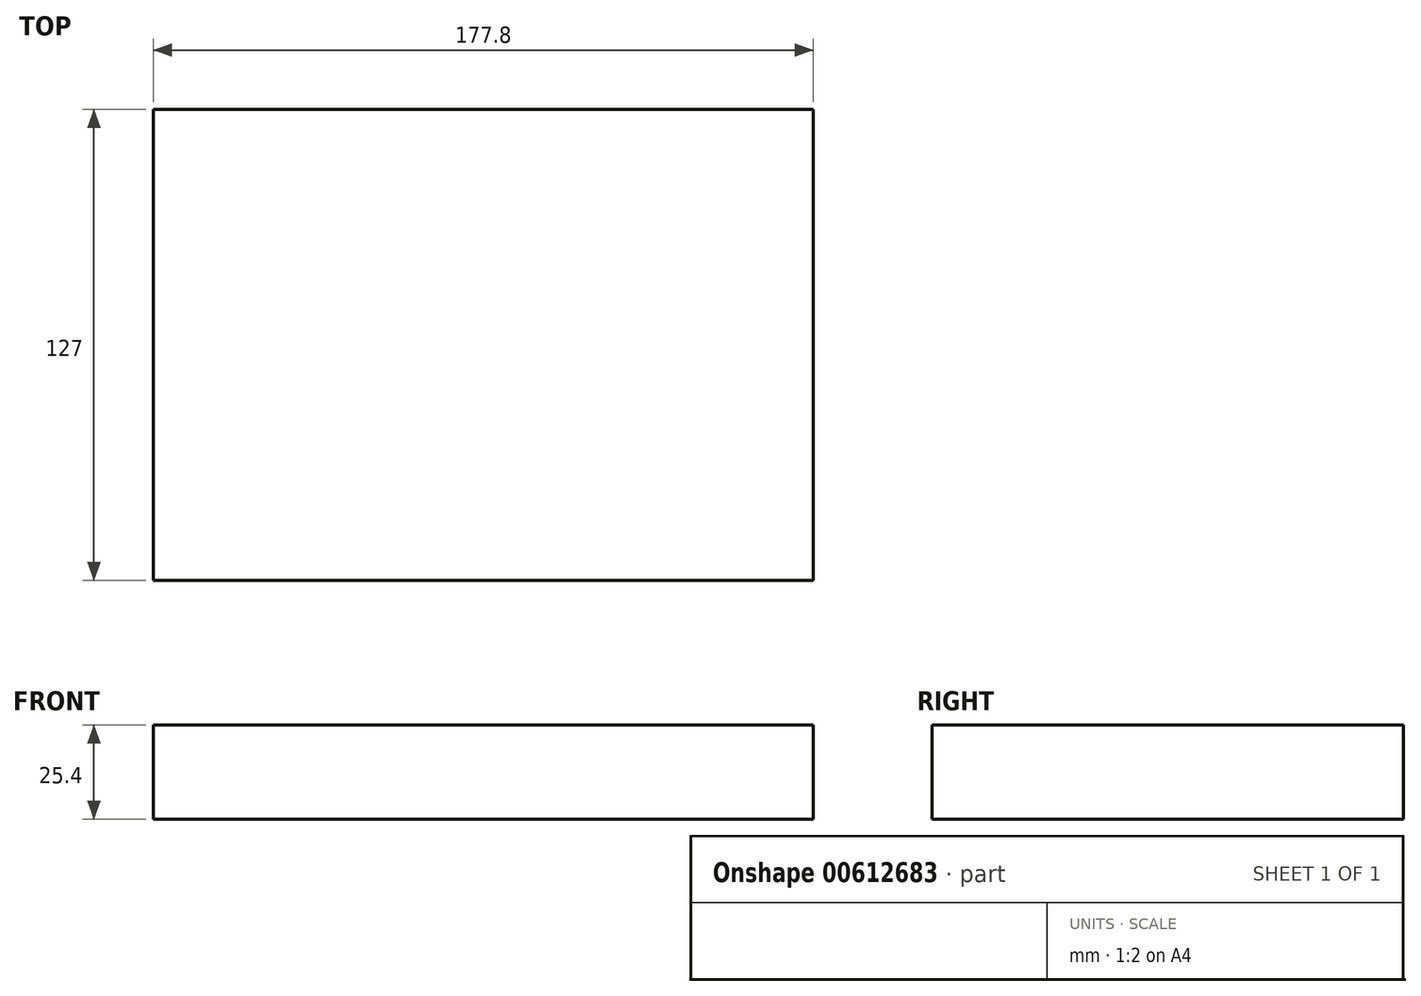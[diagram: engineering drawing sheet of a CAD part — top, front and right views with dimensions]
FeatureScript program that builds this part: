
annotation { "Feature Type Name" : "Feature", "Feature Type Description" : "" }
export const myFeature = defineFeature(function(context is Context, id is Id, definition is map)
    precondition{}
    {
        {
            var Q0;
            Q0=qCreatedBy(makeId("Top.planeOp"),FACE);
            var sketch = newSketch(context, id + "F0", { "sketchPlane" : qUnion([Q0])});
            skLineSegment(sketch, "E0.bottom", {"start": v(88.9, 63.5) * mm, "end": v(-88.9, 63.5) * mm});
            skLineSegment(sketch, "E0.top", {"start": v(88.9, -63.5) * mm, "end": v(-88.9, -63.5) * mm});
            skLineSegment(sketch, "E0.left", {"start": v(88.9, 63.5) * mm, "end": v(88.9, -63.5) * mm});
            skLineSegment(sketch, "E0.right", {"start": v(-88.9, 63.5) * mm, "end": v(-88.9, -63.5) * mm});
            skPoint(sketch, "E0.middle", {"position": v(0, 0) * mm});
            skSolve(sketch);
        }
        {
            var Q0;
            Q0=makeQuery(id+"F0.imprint","IMPRINT",FACE,{"disambiguationData":[TD([[makeQuery(id+"F0.imprint","IMPRINT",EDGE,{"derivedFrom":sQuery(id+"F0.wireOp",EDGE,"E0.bottom")}),1.0]])]});
            extrude(context, id + "F1", {"entities" : qUnion([Q0]), "depth" : 25.4 * mm, "offsetDistance" : 25.4 * mm});
        }
    });
